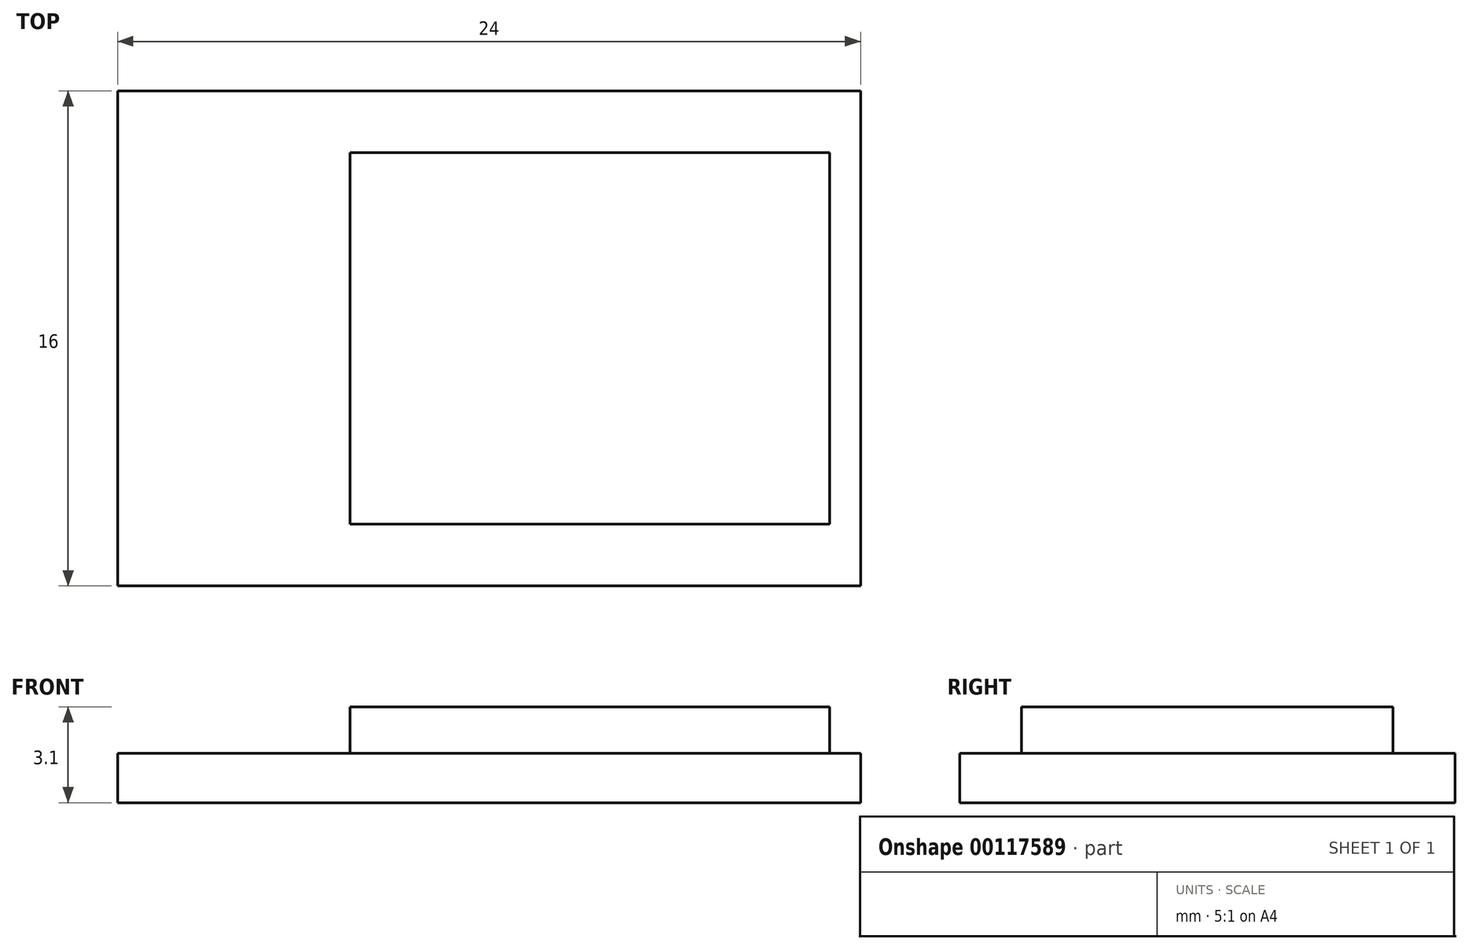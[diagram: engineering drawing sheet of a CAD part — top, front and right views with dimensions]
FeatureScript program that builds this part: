
annotation { "Feature Type Name" : "Feature", "Feature Type Description" : "" }
export const myFeature = defineFeature(function(context is Context, id is Id, definition is map)
    precondition{}
    {
        {
            var Q0;
            Q0=qCreatedBy(makeId("Front.planeOp"),FACE);
            var sketch = newSketch(context, id + "F0", { "sketchPlane" : qUnion([Q0])});
            skLineSegment(sketch, "E0.bottom", {"start": v(-12, 0) * mm, "end": v(12, 0) * mm});
            skLineSegment(sketch, "E0.top", {"start": v(-12, 1.6) * mm, "end": v(12, 1.6) * mm});
            skLineSegment(sketch, "E0.left", {"start": v(-12, 0) * mm, "end": v(-12, 1.6) * mm});
            skLineSegment(sketch, "E0.right", {"start": v(12, 0) * mm, "end": v(12, 1.6) * mm});
            skSolve(sketch);
        }
        {
            var Q0;
            Q0=makeQuery(id+"F0.imprint","IMPRINT",FACE,{"disambiguationData":[TD([[makeQuery(id+"F0.imprint","IMPRINT",EDGE,{"derivedFrom":sQuery(id+"F0.wireOp",EDGE,"E0.bottom")}),1.0]])]});
            extrude(context, id + "F1", {"entities" : qUnion([Q0]), "endBound" : BoundingType.SYMMETRIC, "depth" : 16 * mm});
        }
        {
            var Q0;
            Q0=makeQuery(id+"F1.opExtrude","SWEPT_FACE",FACE,{"disambiguationData":[OSD([sQuery(id+"F0.wireOp",EDGE,"E0.top")])]});
            var sketch = newSketch(context, id + "F2", { "sketchPlane" : qUnion([Q0])});
            skLineSegment(sketch, "E1.bottom", {"start": v(-4.5, 6) * mm, "end": v(11, 6) * mm});
            skLineSegment(sketch, "E1.top", {"start": v(-4.5, -6) * mm, "end": v(11, -6) * mm});
            skLineSegment(sketch, "E1.left", {"start": v(-4.5, 6) * mm, "end": v(-4.5, -6) * mm});
            skLineSegment(sketch, "E1.right", {"start": v(11, 6) * mm, "end": v(11, -6) * mm});
            skLineSegment(sketch, "E2", {"start": v(-12, 0) * mm, "end": v(12, 0) * mm, "construction": true});
            skLineSegment(sketch, "E3", {"start": v(-4.5, 6) * mm, "end": v(-4.5, 8) * mm, "construction": true});
            skLineSegment(sketch, "E4", {"start": v(-4.5, -6) * mm, "end": v(-4.5, -8) * mm, "construction": true});
            skSolve(sketch);
        }
        {
            var Q0;
            Q0=makeQuery(id+"F2.imprint","IMPRINT",FACE,{"disambiguationData":[TD([[makeQuery(id+"F2.imprint","IMPRINT",EDGE,{"derivedFrom":sQuery(id+"F2.wireOp",EDGE,"E1.bottom")}),-1.0]])]});
            extrude(context, id + "F3", {"entities" : qUnion([Q0]), "operationType" : NewBodyOperationType.ADD, "depth" : 1.5 * mm});
        }
    });
